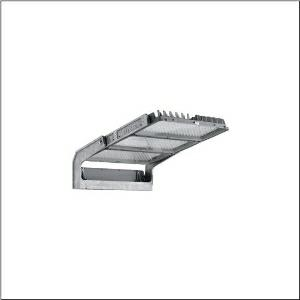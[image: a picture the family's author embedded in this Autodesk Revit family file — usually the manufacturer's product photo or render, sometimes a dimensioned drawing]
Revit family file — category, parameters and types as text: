
# Revit family: floodlight_fl_11_maxi_pro_remote___rs07_5xa779224k01gb_72aa
name_source: partatom
category: Lighting Fixtures
units: mm (PartAtom-declared; Revit-internal decimal feet)

## family parameters
Cut with Voids When Loaded = No
Host = Face
Light Source = No
Part Type = Normal
Room Calculation Point = No
Round Connector Dimension = Use Diameter
Shared = No

## types (1)
- --- (1 x LED, 123000 lm, 1227.1 W, 5700K)
    Apparent Load = 1227 VA
    CIE Flux Codes = 80 93 99 100 99
    Color Rendering = 90
    Color Temperature = 5700K
    Default Elevation = 1800 mm
    Description = Floodlight FL 11  maxi  pro Remote floodlight; light control with lens of PMMA; cover panel of toughened safety glass, transparent; light distribution: RS07, rotationally symmetric direct distribution, LEDcolour temperature: 5700K, rated luminous flux: 123.000lm, colour rendering: CRI > 90, light colour: 957; luminous efficacy: 100lm/W; brightness control: DMX+RDM; with terminal, 8-pole, max. 2.5mm², mains connection: 220..240V/380..400V AC, 50/60Hz, surge voltage resistance: line to ground: 10kV, service life up to 100,000h L90. Typical operating time: 1000h per year, ECG replaceable separately, LED unit replaceable without ESD environment, dustproof LED module, dimming range 10..100%; 1227W floodlight with 3x LED unit of diecast aluminium, coated grey; length: 1.003mm / width: 651mm / height: 338mm; mounting bracket, of diecast aluminium, uncoated, natural, protection rating (complete): IP66; insulation class (complete): insulation class I (protective earthing); certification: CE, ENEC, VDE; ball protection: ball impact resistant, only for outdoor installations in the designated locations, permissible operating ambient temperature: -45..+55°C, permissible storage temperature: -40..+85°Cpackaging unit: 1 piece

Light Distribution: RS07
    Height = 320 mm
    Lamp = 1 x LED
    Lamp Light Flux = 123000 lm
    Lamp Power = 1227.1 W
    Lamp count = 1
    Length = 1002 mm
    Luminous efficacy = 100 lm/W
    Manufacturer = Siteco
    ModVariant = No
    Model = 5XA779224K01GB
    Mounting Place = Ceiling
    Mounting Type = Surface mounted
    Number of Poles = 1
    OnlyDefault = Yes
    Power Factor = 1
    Product Name = Floodlight FL 11 maxi pro Remote | RS07
    Product group = floodlight | ceiling mounted
    ProductGroupID = 301
    Protection Class = Protection class I
    Protection Degree = IP 66
    RLX_Detail_Level = 1
    RLX_Emergency_Light_Flux = 0 lm
    RLX_Emergency_Type = 0
    RLX_Emergency_Type_DB = No
    RlxData = <blob elided: 40373 chars, md5=ae14b8f3>
    Socket = socket
    Standby Power = 0 W
    System Light Flux = 123000 lm
    System Power = 1227 W
    Type Comments = factory setting: luminous flux: 100 % | dim-lin: 255 | 840 mA
    Type Image = l_1356210.jpg
    URL = http://relux.com
    VarID = @adj_013965
    Voltage = 0 V
    Weight = 0.00 kg
    Width = 655 mm

## geometry (parser evidence)
native form markers: Blend x4, Sweep x12
no freeform markers — native parametric forms only
